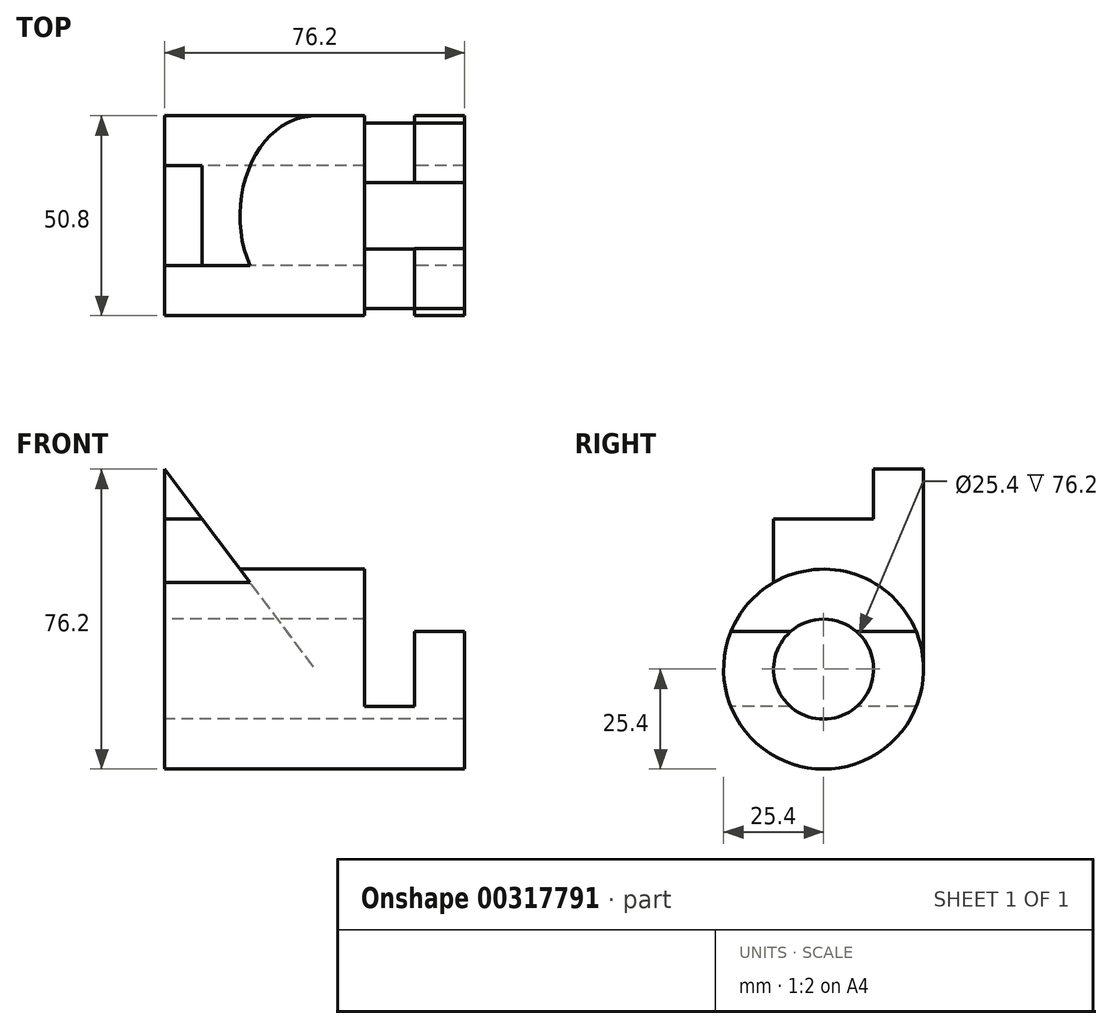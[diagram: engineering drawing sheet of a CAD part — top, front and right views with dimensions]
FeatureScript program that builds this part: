
annotation { "Feature Type Name" : "Feature", "Feature Type Description" : "" }
export const myFeature = defineFeature(function(context is Context, id is Id, definition is map)
    precondition{}
    {
        {
            var Q0;
            Q0=qCreatedBy(makeId("Right.planeOp"),FACE);
            var sketch = newSketch(context, id + "F0", { "sketchPlane" : qUnion([Q0])});
            skCircle(sketch, "E0", {"center": v(0, 0) * mm, "radius": 12.7 * mm});
            skCircle(sketch, "E1", {"center": v(0, 0) * mm, "radius": 25.4 * mm});
            skLineSegment(sketch, "E2", {"start": v(1.31, 25.37) * mm, "end": v(-74.34, 25.37) * mm, "construction": true});
            skSolve(sketch);
        }
        {
            var Q0;
            Q0 = qSketchRegion(id + "F0", true);
            extrude(context, id + "F1", {"entities" : qUnion([Q0]), "depth" : 76.2 * mm});
        }
        {
            var Q0;
            Q0=qCreatedBy(makeId("Right.planeOp"),FACE);
            var sketch = newSketch(context, id + "F2", { "sketchPlane" : qUnion([Q0])});
            skLineSegment(sketch, "E3", {"start": v(-12.7, 22) * mm, "end": v(-12.7, 38.1) * mm});
            skLineSegment(sketch, "E4", {"start": v(-12.7, 38.1) * mm, "end": v(12.7, 38.1) * mm});
            skLineSegment(sketch, "E5", {"start": v(12.7, 38.1) * mm, "end": v(12.7, 50.8) * mm});
            skLineSegment(sketch, "E6", {"start": v(12.7, 50.8) * mm, "end": v(25.4, 50.8) * mm});
            skLineSegment(sketch, "E7", {"start": v(25.4, 50.8) * mm, "end": v(25.4, 0) * mm});
            skArc(sketch, "E8", {"start": v(-12.7, 22) * mm, "mid": v(12.7, 22) * mm, "end": v(25.4, 0) * mm});
            skSolve(sketch);
        }
        {
            var Q0;
            Q0=qCreatedBy(makeId("Front.planeOp"),FACE);
            var sketch = newSketch(context, id + "F3", { "sketchPlane" : qUnion([Q0])});
            skLineSegment(sketch, "E9", {"start": v(0, 0) * mm, "end": v(0, 50.8) * mm});
            skLineSegment(sketch, "E10", {"start": v(0, 50.8) * mm, "end": v(38.1, 0) * mm});
            skLineSegment(sketch, "E11", {"start": v(38.1, 0) * mm, "end": v(0, 0) * mm});
            skSolve(sketch);
        }
        {
            var Q0;
            Q0 = qSketchRegion(id + "F3", true);
            extrude(context, id + "F4", {"entities" : qUnion([Q0]), "operationType" : NewBodyOperationType.ADD, "oppositeDirection" : true, "depth" : 25.4 * mm, "hasSecondDirection" : true, "secondDirectionOppositeDirection" : false, "secondDirectionDepth" : 12.7 * mm});
        }
        {
            var Q0;
            Q0=makeQuery(id+"F1.opExtrude","CAP_FACE",FACE,{"disambiguationData":[OSD([sQuery(id+"F0.wireOp",EDGE,"E0"),sQuery(id+"F0.wireOp",EDGE,"E1")])],"isStart":false});
            var sketch = newSketch(context, id + "F5", { "sketchPlane" : qUnion([Q0])});
            skCircle(sketch, "E12", {"center": v(0, 0) * mm, "radius": 12.7 * mm});
            skSolve(sketch);
        }
        {
            var Q0;
            Q0 = qSketchRegion(id + "F5", true);
            extrude(context, id + "F6", {"entities" : qUnion([Q0]), "operationType" : NewBodyOperationType.REMOVE, "endBound" : BoundingType.THROUGH_ALL, "oppositeDirection" : true, "depth" : 25.4 * mm});
        }
        {
            var Q0;
            Q0=makeQuery(id+"F2.imprint","IMPRINT",FACE,{"disambiguationData":[TD([[makeQuery(id+"F2.imprint","IMPRINT",EDGE,{"derivedFrom":sQuery(id+"F2.wireOp",EDGE,"E3")}),-1.0]])]});
            var sketch = newSketch(context, id + "F7", { "sketchPlane" : qUnion([Q0])});
            skLineSegment(sketch, "E13.bottom", {"start": v(12.7, 38.1) * mm, "end": v(-12.7, 38.1) * mm});
            skLineSegment(sketch, "E13.top", {"start": v(12.7, 50.8) * mm, "end": v(-12.7, 50.8) * mm});
            skLineSegment(sketch, "E13.left", {"start": v(12.7, 38.1) * mm, "end": v(12.7, 50.8) * mm});
            skLineSegment(sketch, "E13.right", {"start": v(-12.7, 38.1) * mm, "end": v(-12.7, 50.8) * mm});
            skSolve(sketch);
        }
        {
            var Q0;
            Q0 = qSketchRegion(id + "F7", true);
            extrude(context, id + "F8", {"entities" : qUnion([Q0]), "operationType" : NewBodyOperationType.REMOVE, "endBound" : BoundingType.THROUGH_ALL, "depth" : 25.4 * mm});
        }
        {
            var Q0;
            Q0=qCreatedBy(makeId("Front.planeOp"),FACE);
            var sketch = newSketch(context, id + "F9", { "sketchPlane" : qUnion([Q0])});
            skLineSegment(sketch, "E14", {"start": v(50.8, 25.4) * mm, "end": v(50.8, -9.52) * mm});
            skLineSegment(sketch, "E15", {"start": v(50.8, -9.52) * mm, "end": v(63.5, -9.52) * mm});
            skLineSegment(sketch, "E16", {"start": v(63.5, -9.52) * mm, "end": v(63.5, 9.53) * mm});
            skLineSegment(sketch, "E17", {"start": v(63.5, 9.53) * mm, "end": v(76.2, 9.53) * mm});
            skLineSegment(sketch, "E18", {"start": v(76.2, 9.53) * mm, "end": v(76.2, 25.4) * mm});
            skLineSegment(sketch, "E19", {"start": v(76.2, 25.4) * mm, "end": v(50.8, 25.4) * mm});
            skSolve(sketch);
        }
        {
            var Q0;
            Q0 = qSketchRegion(id + "F9", true);
            extrude(context, id + "F10", {"entities" : qUnion([Q0]), "operationType" : NewBodyOperationType.REMOVE, "oppositeDirection" : true, "depth" : 25.4 * mm, "hasSecondDirection" : true, "secondDirectionOppositeDirection" : false, "secondDirectionDepth" : 25.4 * mm});
        }
    });
